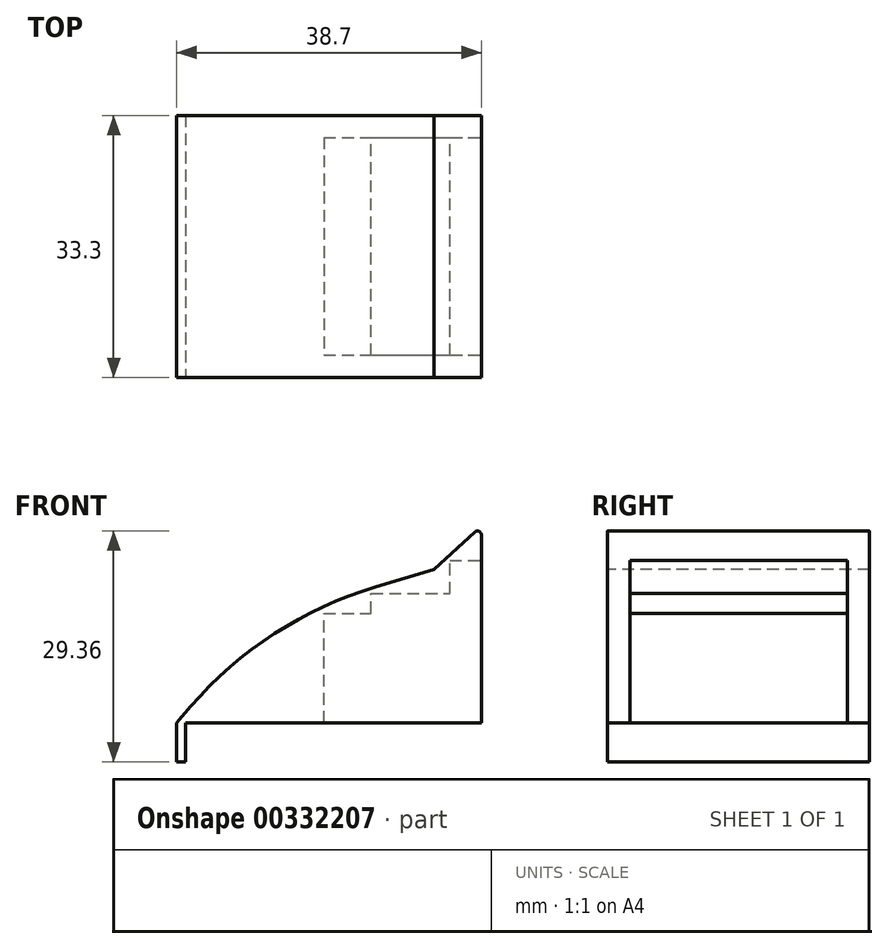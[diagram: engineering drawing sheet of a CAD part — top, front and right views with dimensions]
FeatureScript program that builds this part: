
annotation { "Feature Type Name" : "Feature", "Feature Type Description" : "" }
export const myFeature = defineFeature(function(context is Context, id is Id, definition is map)
    precondition{}
    {
        {
            var Q0;
            Q0=qCreatedBy(makeId("Top.planeOp"),FACE);
            var sketch = newSketch(context, id + "F0", { "sketchPlane" : qUnion([Q0])});
            skLineSegment(sketch, "E0.bottom", {"start": v(-14.4, 11.25) * mm, "end": v(24.3, 11.25) * mm});
            skLineSegment(sketch, "E0.top", {"start": v(-14.4, -22.05) * mm, "end": v(24.3, -22.05) * mm});
            skLineSegment(sketch, "E0.left", {"start": v(-14.4, 11.25) * mm, "end": v(-14.4, -22.05) * mm});
            skLineSegment(sketch, "E0.right", {"start": v(24.3, 11.25) * mm, "end": v(24.3, -22.05) * mm});
            skSolve(sketch);
        }
        {
            var Q0;
            Q0=makeQuery(id+"F0.imprint","IMPRINT",FACE,{"disambiguationData":[TD([[makeQuery(id+"F0.imprint","IMPRINT",EDGE,{"derivedFrom":sQuery(id+"F0.wireOp",EDGE,"E0.bottom")}),-1.0]])]});
            extrude(context, id + "F1", {"entities" : qUnion([Q0]), "depth" : 25 * mm});
        }
        {
            var Q0;
            Q0=makeQuery(id+"F1.opExtrude","SWEPT_FACE",FACE,{"disambiguationData":[OSD([sQuery(id+"F0.wireOp",EDGE,"E0.top")])]});
            var sketch = newSketch(context, id + "F2", { "sketchPlane" : qUnion([Q0])});
            skLineSegment(sketch, "E1", {"start": v(-14.4, 0) * mm, "end": v(-3.1, 13.07) * mm});
            skLineSegment(sketch, "E2", {"start": v(-3.1, 13.07) * mm, "end": v(18.28, 19.48) * mm});
            skLineSegment(sketch, "E3", {"start": v(18.28, 19.48) * mm, "end": v(24.3, 25) * mm});
            skLineSegment(sketch, "E4", {"start": v(24.3, 25) * mm, "end": v(24.3, 0) * mm});
            skLineSegment(sketch, "E5", {"start": v(24.3, 0) * mm, "end": v(-14.4, 0) * mm});
            skSolve(sketch);
        }
        {
            var Q0;
            Q0=makeQuery(id+"F2.imprint","IMPRINT",FACE,{"disambiguationData":[TD([[makeQuery(id+"F2.imprint","IMPRINT",EDGE,{"derivedFrom":sQuery(id+"F2.wireOp",EDGE,"E1")}),1.0]])]});
            extrude(context, id + "F3", {"entities" : qUnion([Q0]), "operationType" : NewBodyOperationType.REMOVE, "endBound" : BoundingType.THROUGH_ALL, "oppositeDirection" : true, "depth" : 25 * mm});
        }
        {
            var Q0;
            Q0=makeQuery(id+"F3.boolean.opBoolean","COPY",EDGE,{"derivedFrom":makeQuery(id+"F3.opExtrude","SWEPT_EDGE",EDGE,{"disambiguationData":[OSD([sQuery(id+"F2.wireOp",EDGE,"E1"),sQuery(id+"F2.wireOp",EDGE,"E2")])]})});
            fillet(context, id + "F4", {"entities" : qUnion([Q0]), "radius" : 50 * mm, "tangentPropagation" : true, "allowEdgeOverflow" : false});
        }
        {
            var Q0;
            Q0=makeQuery(id+"F3.boolean.opBoolean","MERGE",EDGE,{"derivedFrom":[makeQuery(id+"F1.opExtrude","CAP_EDGE",EDGE,{"disambiguationData":[OSD([sQuery(id+"F0.wireOp",EDGE,"E0.right")])],"isStart":false}),makeQuery(id+"F3.opExtrude","SWEPT_EDGE",EDGE,{"disambiguationData":[OSD([sQuery(id+"F0.wireOp",EDGE,"E0.top"),sQuery(id+"F2.wireOp",EDGE,"E3"),sQuery(id+"F2.wireOp",EDGE,"E4")])]})]});
            fillet(context, id + "F5", {"entities" : qUnion([Q0]), "radius" : 0.5 * mm, "tangentPropagation" : true, "allowEdgeOverflow" : false});
        }
        {
            var Q0;
            Q0=makeQuery(id+"F1.opExtrude","SWEPT_FACE",FACE,{"disambiguationData":[OSD([sQuery(id+"F0.wireOp",EDGE,"E0.right")])]});
            var sketch = newSketch(context, id + "F6", { "sketchPlane" : qUnion([Q0])});
            skLineSegment(sketch, "E6", {"start": v(-19.2, 0) * mm, "end": v(-19.2, 20.63) * mm});
            skLineSegment(sketch, "E7", {"start": v(-19.2, 20.63) * mm, "end": v(8.45, 20.63) * mm});
            skLineSegment(sketch, "E8", {"start": v(8.45, 20.63) * mm, "end": v(8.45, 0) * mm});
            skLineSegment(sketch, "E9", {"start": v(8.45, 0) * mm, "end": v(-19.2, 0) * mm});
            skSolve(sketch);
        }
        {
            var Q0;
            Q0=makeQuery(id+"F6.imprint","IMPRINT",FACE,{"disambiguationData":[TD([[makeQuery(id+"F6.imprint","IMPRINT",EDGE,{"derivedFrom":sQuery(id+"F6.wireOp",EDGE,"E6")}),-1.0]])]});
            extrude(context, id + "F7", {"entities" : qUnion([Q0]), "operationType" : NewBodyOperationType.REMOVE, "oppositeDirection" : true, "depth" : 4 * mm});
        }
        {
            var Q0;
            Q0=makeQuery(id+"F7.boolean.opBoolean","COPY",FACE,{"derivedFrom":makeQuery(id+"F7.opExtrude","CAP_FACE",FACE,{"disambiguationData":[OSD([sQuery(id+"F6.wireOp",EDGE,"E6"),sQuery(id+"F6.wireOp",EDGE,"E7"),sQuery(id+"F6.wireOp",EDGE,"E8"),sQuery(id+"F6.wireOp",EDGE,"E9")])],"isStart":false})});
            var sketch = newSketch(context, id + "F8", { "sketchPlane" : qUnion([Q0])});
            skLineSegment(sketch, "E10", {"start": v(-19.2, 0) * mm, "end": v(-19.2, 16.41) * mm});
            skLineSegment(sketch, "E11", {"start": v(-19.2, 16.41) * mm, "end": v(8.45, 16.41) * mm});
            skLineSegment(sketch, "E12", {"start": v(8.45, 16.41) * mm, "end": v(8.45, 0) * mm});
            skLineSegment(sketch, "E13", {"start": v(8.45, 0) * mm, "end": v(-19.2, 0) * mm});
            skSolve(sketch);
        }
        {
            var Q0;
            Q0=makeQuery(id+"F8.imprint","IMPRINT",FACE,{"disambiguationData":[TD([[makeQuery(id+"F8.imprint","IMPRINT",EDGE,{"derivedFrom":sQuery(id+"F8.wireOp",EDGE,"E10")}),-1.0]])]});
            extrude(context, id + "F9", {"entities" : qUnion([Q0]), "operationType" : NewBodyOperationType.REMOVE, "oppositeDirection" : true, "depth" : 10 * mm});
        }
        {
            var Q0;
            Q0=makeQuery(id+"F9.boolean.opBoolean","COPY",FACE,{"derivedFrom":makeQuery(id+"F9.opExtrude","CAP_FACE",FACE,{"disambiguationData":[OSD([sQuery(id+"F8.wireOp",EDGE,"E10"),sQuery(id+"F8.wireOp",EDGE,"E11"),sQuery(id+"F8.wireOp",EDGE,"E12"),sQuery(id+"F8.wireOp",EDGE,"E13")])],"isStart":false})});
            var sketch = newSketch(context, id + "F10", { "sketchPlane" : qUnion([Q0])});
            skLineSegment(sketch, "E14", {"start": v(-19.2, 0) * mm, "end": v(-19.2, 13.9) * mm});
            skLineSegment(sketch, "E15", {"start": v(-19.2, 13.9) * mm, "end": v(8.45, 13.9) * mm});
            skLineSegment(sketch, "E16", {"start": v(8.45, 13.9) * mm, "end": v(8.45, 0) * mm});
            skLineSegment(sketch, "E17", {"start": v(8.45, 0) * mm, "end": v(-19.2, 0) * mm});
            skSolve(sketch);
        }
        {
            var Q0;
            Q0=makeQuery(id+"F10.imprint","IMPRINT",FACE,{"disambiguationData":[TD([[makeQuery(id+"F10.imprint","IMPRINT",EDGE,{"derivedFrom":sQuery(id+"F10.wireOp",EDGE,"E14")}),-1.0]])]});
            extrude(context, id + "F11", {"entities" : qUnion([Q0]), "operationType" : NewBodyOperationType.REMOVE, "oppositeDirection" : true, "depth" : 6 * mm});
        }
        {
            var Q0;
            Q0=makeQuery(id+"F1.opExtrude","CAP_FACE",FACE,{"disambiguationData":[OSD([sQuery(id+"F0.wireOp",EDGE,"E0.bottom"),sQuery(id+"F0.wireOp",EDGE,"E0.top"),sQuery(id+"F0.wireOp",EDGE,"E0.left"),sQuery(id+"F0.wireOp",EDGE,"E0.right")])],"isStart":true});
            var sketch = newSketch(context, id + "F12", { "sketchPlane" : qUnion([Q0])});
            skLineSegment(sketch, "E18.bottom", {"start": v(-14.4, -11.25) * mm, "end": v(-13.3, -11.25) * mm});
            skLineSegment(sketch, "E18.top", {"start": v(-14.4, 22.05) * mm, "end": v(-13.3, 22.05) * mm});
            skLineSegment(sketch, "E18.left", {"start": v(-14.4, -11.25) * mm, "end": v(-14.4, 22.05) * mm});
            skLineSegment(sketch, "E18.right", {"start": v(-13.3, -11.25) * mm, "end": v(-13.3, 22.05) * mm});
            skSolve(sketch);
        }
        {
            var Q0;
            Q0=makeQuery(id+"F12.imprint","IMPRINT",FACE,{"disambiguationData":[TD([[makeQuery(id+"F12.imprint","IMPRINT",EDGE,{"derivedFrom":sQuery(id+"F12.wireOp",EDGE,"E18.bottom")}),1.0]])]});
            extrude(context, id + "F13", {"entities" : qUnion([Q0]), "operationType" : NewBodyOperationType.ADD, "depth" : 5 * mm});
        }
    });
